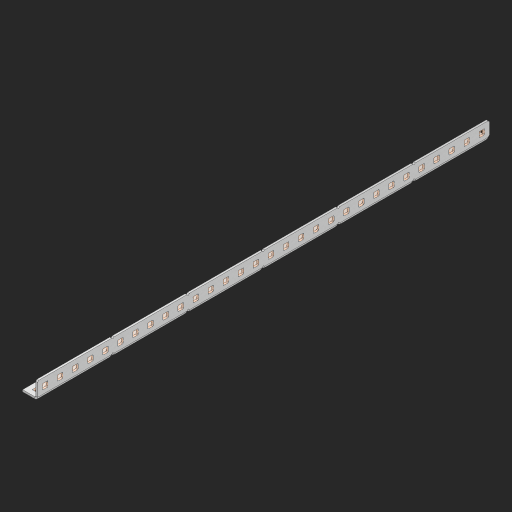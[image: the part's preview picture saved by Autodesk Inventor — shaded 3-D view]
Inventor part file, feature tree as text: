
AUTODESK INVENTOR PART (.ipt)
format: ipt  version: 2023 (Build 270158000, 158)  size: 973,312 bytes
history: native  units: in
note: dims shown in document units (in); Inventor stores cm internally (conversion verified against a paired STEP export)
features: other x65, extrude x59, sheet_metal_op x10, sketch x8, mirror x1, pattern_linear x1, chamfer x1
ambient origin geometry x8: Origin, YZ Plane, XZ Plane, XY Plane, X Axis, Y Axis, Z Axis, Center Point
bodies: Solid1 (feature_tree), Body (feature_tree)
feature tree (145):
  other  "Flange Pattern Plane"
  sheet_metal_op  "Flange Pattern"
  sheet_metal_op  "Body Pattern"
  other  "Arc Length"
  mirror  "Notch Mirror"
  pattern_linear  "Notch Pattern"  Spacing1=0.25in  [1 undecoded]
  chamfer  "End Chamfer"
  extrude  "Half Cut"  Depth=0.0625in
  sketch  "Sketch1"  dims[d0=1.5in]
  other  "Plate1"
  sketch  "Sketch2"  dims[d1=15.0in]
  other  "Plate2"
  sheet_metal_op  "Bend1"
  sheet_metal_op  "Corner1"
  sketch  "Sketch3"  dims[d2=0.0625in]
  other  "Flange Pattern Sketch"
  sketch  "Sketch7"  dims[d3=0.0625in]
  other  "Srf1"
  other  "Srf2"
  sketch  "Sketch8"  dims[d4=0.0312in]
  sketch  "Sketch9"  dims[d5=0.125in]
  other  "Srf91"
  sheet_metal_op  "Body Pattern Sketch"
  other  "Srf92"
  sketch  "Sketch13"  dims[d6=0.0625in]
  sketch  "Sketch14"  dims[d7=0.5in d8=90.0deg d9=0.0312in d10=0.25in d11=0.0625in d12=0.0625in d16=0.182in d17=0.02in d18=0.0625in d19=0.0in d20=0.25in d21=0.25in d46=0.172in d47=1.0in d48=0.0in d49=0.182in d50=0.02in d51=0.25in d52=0.25in d53=0.0625in d54=0.0in d55=0.172in d56=1.0in d57=0.0in d60=11.811in d62=0.5in d63=0.3937in d65=0.5in d85=0.1473in d86=0.1782in d88=0.04in d89=0.0625in d90=0.0in d91=0.04in d92=0.0491in d95=2.5in d96=0.04in d97=0.25in d98=45.0deg d101=0.0in d102=2.497in d131=0.5in d132=11.811in d134=0.5in d139=0.5in]
  other  "Srf856"
  other  "Srf1310"
  other  "Srf1311"
  other  "Srf1312"
  other  "Srf1376"
  other  "Srf1377"
  other  "Srf1728"
  other  "Srf1755"
  other  "Srf1878"
  other  "Srf1879"
  other  "Srf1880"
  other  "Srf1881"
  other  "Srf1882"
  other  "Srf1883"
  other  "Srf1884"
  other  "Srf1885"
  other  "Srf1886"
  other  "Srf1887"
  other  "Srf1888"
  other  "Srf1889"
  other  "Srf1890"
  other  "Srf1891"
  other  "Srf1892"
  other  "Srf1893"
  other  "Srf1894"
  other  "Srf1895"
  other  "Srf1896"
  other  "Srf1897"
  other  "Srf1898"
  other  "Srf1899"
  other  "Srf1900"
  other  "Srf1901"
  other  "Srf1942"
  other  "Srf1943"
  other  "Srf1944"
  other  "Srf1945"
  other  "Srf1946"
  other  "Srf1947"
  other  "Srf1948"
  other  "Srf1949"
  other  "Srf1950"
  other  "Srf1951"
  other  "Srf1952"
  other  "Srf1953"
  other  "Srf1954"
  other  "Srf1955"
  other  "Srf1956"
  other  "Srf1957"
  other  "Srf1958"
  other  "Srf1959"
  other  "Srf1960"
  other  "Srf1961"
  other  "Srf1962"
  other  "Srf1963"
  other  "Srf1964"
  other  "Srf1965"
  sheet_metal_op  "Flange Stamp"
  sheet_metal_op  "Flange Circle"
  sheet_metal_op  "Body Stamp"
  sheet_metal_op  "Body Circle"
  sheet_metal_op  "Notch"
  extrude  "ExtrusionSrf2"  Depth=0.0625in
  extrude  "ExtrusionSrf92"  Depth=0.5in
  extrude  "ExtrusionSrf856"  Depth=0.02in
  extrude  "ExtrusionSrf1310"  Depth=0.0625in
  extrude  "ExtrusionSrf1311"  TaperAngle=0.0deg  [1 undecoded]
  extrude  "ExtrusionSrf1312"  Depth=0.5in
  extrude  "ExtrusionSrf1376"  Depth=0.5in
  extrude  "ExtrusionSrf1377"  Depth=0.5in
  extrude  "ExtrusionSrf1728"  Depth=0.5in TaperAngle=0.0deg
  extrude  "ExtrusionSrf1755"  Depth=0.5in
  extrude  "ExtrusionSrf1878"  Depth=0.02in
  extrude  "ExtrusionSrf1879"  Depth=0.5in
  extrude  "ExtrusionSrf1880"  Depth=0.5in
  extrude  "ExtrusionSrf1881"  Depth=0.0625in
  extrude  "ExtrusionSrf1882"  TaperAngle=0.0deg  [1 undecoded]
  extrude  "ExtrusionSrf1883"  Depth=0.5in
  extrude  "ExtrusionSrf1884"  Depth=0.5in TaperAngle=0.0deg
  extrude  "ExtrusionSrf1885"  Depth=0.5in
  extrude  "ExtrusionSrf1886"  Depth=0.5in
  extrude  "ExtrusionSrf1887"  Depth=0.5in
  extrude  "ExtrusionSrf1888"  Depth=0.5in
  extrude  "ExtrusionSrf1889"  Depth=0.5in
  extrude  "ExtrusionSrf1890"  Depth=0.0625in
  extrude  "ExtrusionSrf1891"  TaperAngle=0.0deg  [1 undecoded]
  extrude  "ExtrusionSrf1892"  Depth=0.5in
  extrude  "ExtrusionSrf1893"  Depth=0.5in
  extrude  "ExtrusionSrf1894"  Depth=0.5in
  extrude  "ExtrusionSrf1895"  Depth=0.5in TaperAngle=45.0deg
  extrude  "ExtrusionSrf1896"  TaperAngle=0.0deg  [1 undecoded]
  extrude  "ExtrusionSrf1897"  Depth=0.5in
  extrude  "ExtrusionSrf1898"  Depth=0.5in
  extrude  "ExtrusionSrf1899"  Depth=0.5in
  extrude  "ExtrusionSrf1900"  Depth=0.5in
  extrude  "ExtrusionSrf1901"  Depth=0.5in
  extrude  "ExtrusionSrf1942"  [1 undecoded]
  extrude  "ExtrusionSrf1943"  [1 undecoded]
  extrude  "ExtrusionSrf1944"  [1 undecoded]
  extrude  "ExtrusionSrf1945"  [1 undecoded]
  extrude  "ExtrusionSrf1946"  [1 undecoded]
  extrude  "ExtrusionSrf1947"  [1 undecoded]
  extrude  "ExtrusionSrf1948"  [1 undecoded]
  extrude  "ExtrusionSrf1949"  [1 undecoded]
  extrude  "ExtrusionSrf1950"  [1 undecoded]
  extrude  "ExtrusionSrf1951"  [1 undecoded]
  extrude  "ExtrusionSrf1952"  [1 undecoded]
  extrude  "ExtrusionSrf1953"  [1 undecoded]
  extrude  "ExtrusionSrf1954"  [1 undecoded]
  extrude  "ExtrusionSrf1955"  [1 undecoded]
  extrude  "ExtrusionSrf1956"  [1 undecoded]
  extrude  "ExtrusionSrf1957"  [1 undecoded]
  extrude  "ExtrusionSrf1958"  [1 undecoded]
  extrude  "ExtrusionSrf1959"  [1 undecoded]
  extrude  "ExtrusionSrf1960"  [1 undecoded]
  extrude  "ExtrusionSrf1961"  [1 undecoded]
  extrude  "ExtrusionSrf1962"  [1 undecoded]
  extrude  "ExtrusionSrf1963"  [1 undecoded]
  extrude  "ExtrusionSrf1964"  [1 undecoded]
  extrude  "ExtrusionSrf1965"  [1 undecoded]
note: 29 required parameter values undecoded (feature->parameter linkage not recoverable at this tier; creation-order binding heuristic only, values carry confidence <= 0.55)
